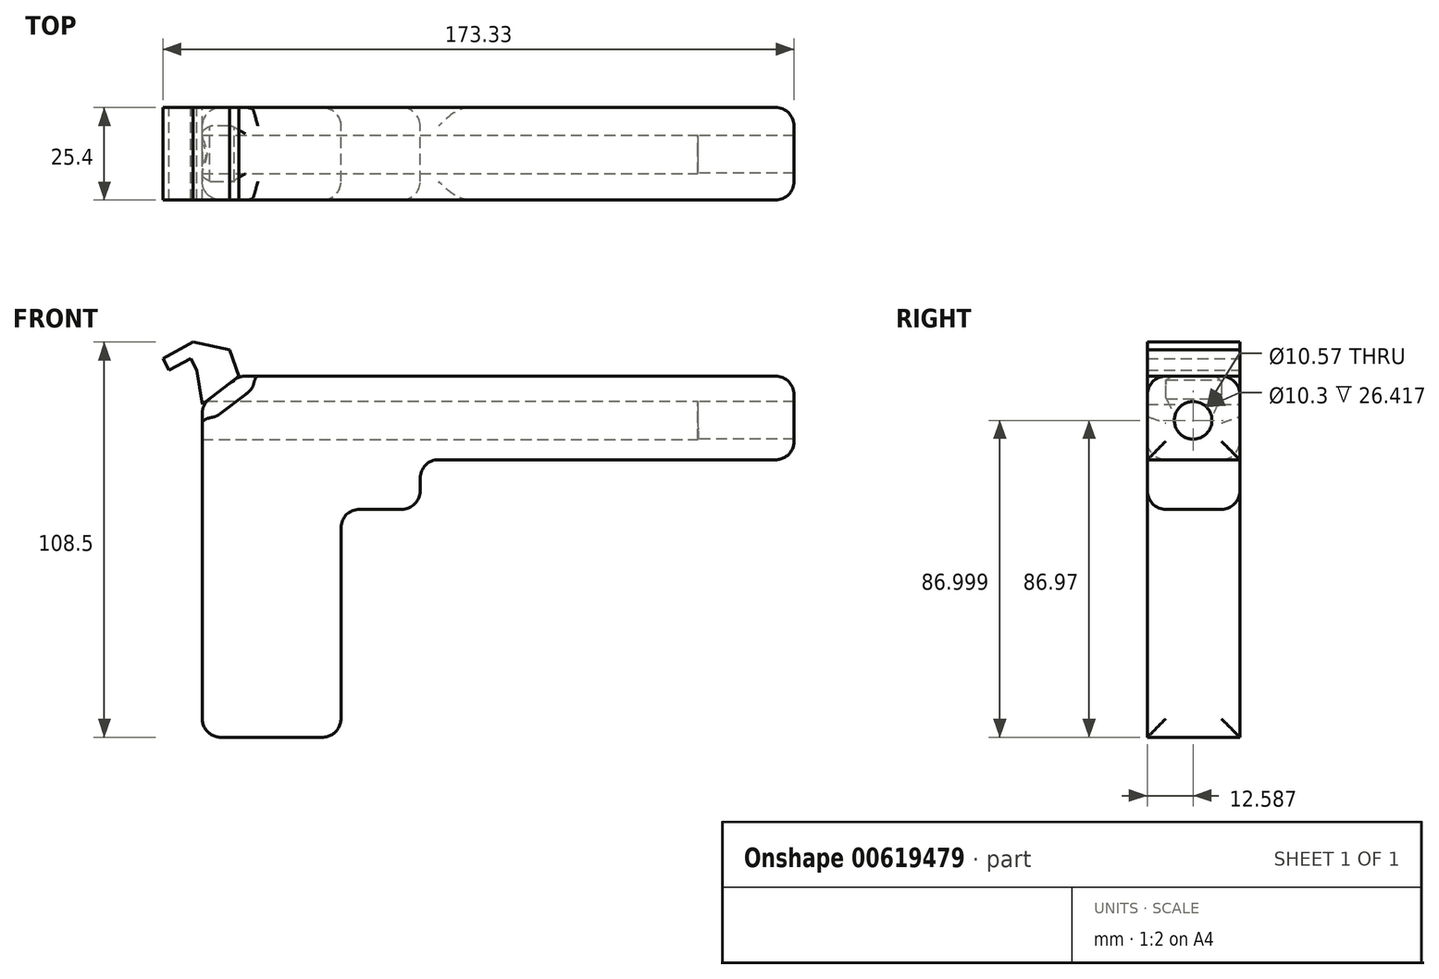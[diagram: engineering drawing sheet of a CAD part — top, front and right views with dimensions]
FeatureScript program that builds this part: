
annotation { "Feature Type Name" : "Feature", "Feature Type Description" : "" }
export const myFeature = defineFeature(function(context is Context, id is Id, definition is map)
    precondition{}
    {
        {
            var Q0;
            Q0=qCreatedBy(makeId("Front.planeOp"),FACE);
            var sketch = newSketch(context, id + "F0", { "sketchPlane" : qUnion([Q0])});
            skLineSegment(sketch, "E0", {"start": v(-59.82, 21.4) * mm, "end": v(-59.82, -54.8) * mm});
            skLineSegment(sketch, "E1", {"start": v(-21.72, -54.8) * mm, "end": v(-59.82, -54.8) * mm});
            skLineSegment(sketch, "E2", {"start": v(-59.82, 21.4) * mm, "end": v(-21.72, 21.4) * mm});
            skLineSegment(sketch, "E3", {"start": v(-59.82, 21.4) * mm, "end": v(-59.82, 36.64) * mm});
            skLineSegment(sketch, "E4", {"start": v(-59.82, 36.64) * mm, "end": v(-49.72, 44.33) * mm});
            skLineSegment(sketch, "E5", {"start": v(-49.72, 44.33) * mm, "end": v(102.68, 44.33) * mm});
            skLineSegment(sketch, "E6", {"start": v(102.68, 44.33) * mm, "end": v(102.68, 21.4) * mm});
            skLineSegment(sketch, "E7", {"start": v(102.68, 21.4) * mm, "end": v(77.28, 21.4) * mm});
            skLineSegment(sketch, "E8", {"start": v(-21.72, 21.4) * mm, "end": v(77.28, 21.4) * mm});
            skLineSegment(sketch, "E9", {"start": v(-19.87, 51.15) * mm, "end": v(-21.72, 51.15) * mm});
            skLineSegment(sketch, "E10", {"start": v(-20.2, 7.79) * mm, "end": v(0, 7.79) * mm});
            skLineSegment(sketch, "E11", {"start": v(0, 7.79) * mm, "end": v(0, 21.4) * mm});
            skLineSegment(sketch, "E12", {"start": v(-21.72, 21.4) * mm, "end": v(-17.5, 10.03) * mm});
            skLineSegment(sketch, "E13", {"start": v(-17.5, 10.03) * mm, "end": v(-14.94, 10.98) * mm});
            skLineSegment(sketch, "E14", {"start": v(-14.94, 10.98) * mm, "end": v(-11.42, 13.47) * mm});
            skLineSegment(sketch, "E15", {"start": v(-21.72, -54.8) * mm, "end": v(-21.72, 21.4) * mm});
            skLineSegment(sketch, "E16", {"start": v(-20.2, 7.79) * mm, "end": v(-21.72, 7.79) * mm});
            skLineSegment(sketch, "E17", {"start": v(-49.72, 44.33) * mm, "end": v(-52.32, 51.56) * mm});
            skLineSegment(sketch, "E18", {"start": v(-52.32, 51.56) * mm, "end": v(-62.32, 53.7) * mm});
            skLineSegment(sketch, "E19", {"start": v(-62.32, 53.7) * mm, "end": v(-70.65, 49.18) * mm});
            skLineSegment(sketch, "E20", {"start": v(-70.65, 49.18) * mm, "end": v(-68.9, 45.97) * mm});
            skLineSegment(sketch, "E21", {"start": v(-68.9, 45.97) * mm, "end": v(-63, 49.18) * mm});
            skLineSegment(sketch, "E22", {"start": v(-63, 49.18) * mm, "end": v(-61.27, 45.97) * mm});
            skLineSegment(sketch, "E23", {"start": v(-61.27, 45.97) * mm, "end": v(-59.82, 36.64) * mm});
            skSolve(sketch);
        }
        {
            var Q0;
            {var subQ0=sQuery(id+"F0.wireOp",EDGE,"E2");Q0=makeQuery(id+"F0.imprint","IMPRINT",FACE,{"disambiguationData":[TD([[makeQuery(id+"F0.imprint","IMPRINT",EDGE,{"derivedFrom":subQ0}),1.0]])]});}
            extrude(context, id + "F1", {"entities" : qUnion([Q0]), "depth" : 25.4 * mm, "offsetDistance" : 25.4 * mm});
        }
        {
            var Q0;
            Q0=makeQuery(id+"F0.imprint","IMPRINT",FACE,{"disambiguationData":[TD([[makeQuery(id+"F0.imprint","IMPRINT",EDGE,{"derivedFrom":sQuery(id+"F0.wireOp",EDGE,"E0")}),1.0]])]});
            extrude(context, id + "F2", {"entities" : qUnion([Q0]), "operationType" : NewBodyOperationType.ADD, "depth" : 25.4 * mm, "offsetDistance" : 25.4 * mm});
        }
        {
            var Q0;
            Q0=makeQuery(id+"F0.imprint","IMPRINT",FACE,{"disambiguationData":[TD([[makeQuery(id+"F0.imprint","IMPRINT",EDGE,{"derivedFrom":sQuery(id+"F0.wireOp",EDGE,"E10")}),1.0]])]});
            extrude(context, id + "F3", {"entities" : qUnion([Q0]), "operationType" : NewBodyOperationType.ADD, "depth" : 25.4 * mm, "offsetDistance" : 25.4 * mm});
        }
        {
            var Q0;
            Q0=makeQuery(id+"F1.opExtrude","CAP_EDGE",EDGE,{"disambiguationData":[OSD([sQuery(id+"F0.wireOp",EDGE,"E6")])],"isStart":true});
            var Q1;
            Q1=makeQuery(id+"F1.opExtrude","SWEPT_EDGE",EDGE,{"disambiguationData":[OSD([sQuery(id+"F0.wireOp",EDGE,"E5"),sQuery(id+"F0.wireOp",EDGE,"E6")])]});
            var Q2;
            Q2=makeQuery(id+"F1.opExtrude","CAP_EDGE",EDGE,{"disambiguationData":[OSD([sQuery(id+"F0.wireOp",EDGE,"E6")])],"isStart":false});
            var Q3;
            Q3=makeQuery(id+"F1.opExtrude","SWEPT_EDGE",EDGE,{"disambiguationData":[OSD([sQuery(id+"F0.wireOp",EDGE,"E6"),sQuery(id+"F0.wireOp",EDGE,"E7")])]});
            fillet(context, id + "F4", {"entities" : qUnion([Q0, Q1, Q2, Q3]), "radius" : 5.08 * mm, "tangentPropagation" : true, "allowEdgeOverflow" : false});
        }
        {
            var Q0;
            Q0=makeQuery(id+"F1.opExtrude","CAP_EDGE",EDGE,{"disambiguationData":[OSD([sQuery(id+"F0.wireOp",EDGE,"E4")])],"isStart":true});
            var Q1;
            Q1=makeQuery(id+"F1.opExtrude","CAP_EDGE",EDGE,{"disambiguationData":[OSD([sQuery(id+"F0.wireOp",EDGE,"E4")])],"isStart":false});
            chamfer(context, id + "F5", {"entities" : qUnion([Q0, Q1]), "width" : 5.08 * mm, "tangentPropagation" : true});
        }
        {
            var Q0;
            Q0=makeQuery(id+"F3.opExtrude","CAP_EDGE",EDGE,{"disambiguationData":[OSD([sQuery(id+"F0.wireOp",EDGE,"E11")])],"isStart":true});
            var Q1;
            Q1=makeQuery(id+"F3.opExtrude","CAP_EDGE",EDGE,{"disambiguationData":[OSD([sQuery(id+"F0.wireOp",EDGE,"E10"),sQuery(id+"F0.wireOp",EDGE,"E16")])],"isStart":true});
            var Q2;
            Q2=makeQuery(id+"F3.opExtrude","CAP_EDGE",EDGE,{"disambiguationData":[OSD([sQuery(id+"F0.wireOp",EDGE,"E11")])],"isStart":false});
            var Q3;
            Q3=makeQuery(id+"F3.opExtrude","CAP_EDGE",EDGE,{"disambiguationData":[OSD([sQuery(id+"F0.wireOp",EDGE,"E10"),sQuery(id+"F0.wireOp",EDGE,"E16")])],"isStart":false});
            var Q4;
            Q4=makeQuery(id+"F3.opExtrude","SWEPT_EDGE",EDGE,{"disambiguationData":[OSD([sQuery(id+"F0.wireOp",EDGE,"E10"),sQuery(id+"F0.wireOp",EDGE,"E11")])]});
            var Q5;
            Q5=makeQuery(id+"F3.opExtrude","SWEPT_FACE",FACE,{"disambiguationData":[OSD([sQuery(id+"F0.wireOp",EDGE,"E11")])]});
            var Q6;
            Q6=makeQuery(id+"F2.opExtrude","SWEPT_FACE",FACE,{"disambiguationData":[OSD([sQuery(id+"F0.wireOp",EDGE,"E15")])]});
            var Q7;
            Q7=makeQuery(id+"F2.boolean.opBoolean","MERGE",FACE,{"derivedFrom":[makeQuery(id+"F1.opExtrude","SWEPT_FACE",FACE,{"disambiguationData":[OSD([sQuery(id+"F0.wireOp",EDGE,"E3")])]}),makeQuery(id+"F2.opExtrude","SWEPT_FACE",FACE,{"disambiguationData":[OSD([sQuery(id+"F0.wireOp",EDGE,"E0")])]})]});
            var Q8;
            Q8=makeQuery(id+"F1.opExtrude","SWEPT_FACE",FACE,{"disambiguationData":[OSD([sQuery(id+"F0.wireOp",EDGE,"E5")])]});
            fillet(context, id + "F6", {"entities" : qUnion([Q0, Q1, Q2, Q3, Q4, Q5, Q6, Q7, Q8]), "radius" : 5.08 * mm, "tangentPropagation" : true, "allowEdgeOverflow" : false});
        }
        {
            var Q0;
            Q0=makeQuery(id+"F1.opExtrude","SWEPT_FACE",FACE,{"disambiguationData":[OSD([sQuery(id+"F0.wireOp",EDGE,"E4")])]});
            var sketch = newSketch(context, id + "F7", { "sketchPlane" : qUnion([Q0])});
            skLineSegment(sketch, "E24.bottom", {"start": v(-14.4, -5.45) * mm, "end": v(-21.74, -5.45) * mm});
            skLineSegment(sketch, "E24.top", {"start": v(-14.4, -20.32) * mm, "end": v(-21.74, -20.32) * mm});
            skLineSegment(sketch, "E24.left", {"start": v(-14.4, -5.45) * mm, "end": v(-14.4, -20.32) * mm});
            skLineSegment(sketch, "E24.right", {"start": v(-21.74, -5.45) * mm, "end": v(-21.74, -20.32) * mm});
            skLineSegment(sketch, "E25", {"start": v(-19, -13.14) * mm, "end": v(-18, -13.14) * mm});
            skPoint(sketch, "E25.endSnap0", {"position": v(-18, -9.1) * mm});
            skLineSegment(sketch, "E26", {"start": v(-18, -13.14) * mm, "end": v(-19, -13.14) * mm});
            skLineSegment(sketch, "E27", {"start": v(-18, -13.14) * mm, "end": v(-19, -12.26) * mm});
            skLineSegment(sketch, "E28", {"start": v(-18, -10.58) * mm, "end": v(-19, -12.26) * mm});
            skLineSegment(sketch, "E29", {"start": v(-18, -10.58) * mm, "end": v(-18, -13.14) * mm});
            skLineSegment(sketch, "E30", {"start": v(-19.53, -10.01) * mm, "end": v(-18, -10.58) * mm});
            skLineSegment(sketch, "E31", {"start": v(-19.72, -10.75) * mm, "end": v(-19, -12.26) * mm});
            skLineSegment(sketch, "E32", {"start": v(-19.33, -11.5) * mm, "end": v(-18, -10.58) * mm});
            skLineSegment(sketch, "E33", {"start": v(-19.33, -11.68) * mm, "end": v(-18, -13.14) * mm});
            skLineSegment(sketch, "E34", {"start": v(-19.91, -14.25) * mm, "end": v(-19.91, -15.54) * mm});
            skLineSegment(sketch, "E35", {"start": v(-19.91, -15.54) * mm, "end": v(-19.91, -14.25) * mm});
            skLineSegment(sketch, "E36", {"start": v(-19.14, -15.37) * mm, "end": v(-19.91, -14.25) * mm});
            skLineSegment(sketch, "E37", {"start": v(-19.14, -15.37) * mm, "end": v(-18, -13.14) * mm});
            skLineSegment(sketch, "E38", {"start": v(-17.78, -14.08) * mm, "end": v(-19.14, -15.37) * mm});
            skLineSegment(sketch, "E39", {"start": v(-17.58, -12.24) * mm, "end": v(-18, -10.58) * mm});
            skLineSegment(sketch, "E40", {"start": v(-19.91, -13.15) * mm, "end": v(-19, -12.26) * mm});
            skLineSegment(sketch, "E41", {"start": v(-20.3, -11.85) * mm, "end": v(-18, -13.14) * mm});
            skSolve(sketch);
        }
        {
            var Q0;
            Q0 = qSketchRegion(id + "F7", true);
            extrude(context, id + "F8", {"entities" : qUnion([Q0]), "operationType" : NewBodyOperationType.ADD, "oppositeDirection" : true, "depth" : 29.72 * mm, "offsetDistance" : 25.4 * mm});
        }
        {
            var Q0;
            Q0=makeQuery(id+"F0.imprint","IMPRINT",FACE,{"disambiguationData":[TD([[makeQuery(id+"F0.imprint","IMPRINT",EDGE,{"derivedFrom":sQuery(id+"F0.wireOp",EDGE,"E4")}),1.0]])]});
            extrude(context, id + "F9", {"entities" : qUnion([Q0]), "operationType" : NewBodyOperationType.ADD, "depth" : 25.4 * mm, "offsetDistance" : 25.4 * mm});
        }
        {
            var Q0;
            Q0=qCreatedBy(makeId("Right.planeOp"),FACE);
            var sketch = newSketch(context, id + "F10", { "sketchPlane" : qUnion([Q0])});
            skCircle(sketch, "E42", {"center": v(-12.81, 32.17) * mm, "radius": 5.28 * mm});
            skSolve(sketch);
        }
        {
            var Q0;
            Q0=sQuery(id+"F10.wireOp",VERTEX,"E42.center");
            var Q1;
            Q1=makeQuery(id+"F1.opExtrude","SWEPT_BODY",BODY,{"disambiguationData":[OSD([sQuery(id+"F0.wireOp",EDGE,"E2"),sQuery(id+"F0.wireOp",EDGE,"E3"),sQuery(id+"F0.wireOp",EDGE,"E4"),sQuery(id+"F0.wireOp",EDGE,"E5"),sQuery(id+"F0.wireOp",EDGE,"E6"),sQuery(id+"F0.wireOp",EDGE,"E7"),sQuery(id+"F0.wireOp",EDGE,"E8")])]});
            hole(context, id + "F11", {"style" : HoleStyle.SIMPLE, "endStyle" : HoleEndStyle.BLIND, "holeDiameter" : 10.57 * mm, "majorDiameter" : 6.35 * mm, "holeDepth" : 76.2 * mm, "isTappedThrough" : true, "tappedDepth" : 12.7 * mm, "tapClearance" : 3, "locations" : qUnion([Q0]), "scope" : qUnion([Q1])});
        }
        {
            var Q0;
            Q0=sQuery(id+"F10.wireOp",VERTEX,"E42.center");
            var Q1;
            Q1=makeQuery(id+"F1.opExtrude","SWEPT_BODY",BODY,{"disambiguationData":[OSD([sQuery(id+"F0.wireOp",EDGE,"E2"),sQuery(id+"F0.wireOp",EDGE,"E3"),sQuery(id+"F0.wireOp",EDGE,"E4"),sQuery(id+"F0.wireOp",EDGE,"E5"),sQuery(id+"F0.wireOp",EDGE,"E6"),sQuery(id+"F0.wireOp",EDGE,"E7"),sQuery(id+"F0.wireOp",EDGE,"E8")])]});
            hole(context, id + "F12", {"style" : HoleStyle.SIMPLE, "endStyle" : HoleEndStyle.BLIND, "oppositeDirection" : true, "holeDiameter" : 10.57 * mm, "majorDiameter" : 6.35 * mm, "holeDepth" : 76.2 * mm, "isTappedThrough" : true, "tappedDepth" : 12.7 * mm, "tapClearance" : 3, "locations" : qUnion([Q0]), "scope" : qUnion([Q1])});
        }
        {
            var Q0;
            Q0=qCreatedBy(makeId("Right.planeOp"),FACE);
            var sketch = newSketch(context, id + "F13", { "sketchPlane" : qUnion([Q0])});
            skCircle(sketch, "E43", {"center": v(-12.81, 32.2) * mm, "radius": 5.27 * mm});
            skSolve(sketch);
        }
        {
            var Q0;
            Q0=sQuery(id+"F13.wireOp",VERTEX,"E43.center");
            var Q1;
            Q1=makeQuery(id+"F1.opExtrude","SWEPT_BODY",BODY,{"disambiguationData":[OSD([sQuery(id+"F0.wireOp",EDGE,"E2"),sQuery(id+"F0.wireOp",EDGE,"E3"),sQuery(id+"F0.wireOp",EDGE,"E4"),sQuery(id+"F0.wireOp",EDGE,"E5"),sQuery(id+"F0.wireOp",EDGE,"E6"),sQuery(id+"F0.wireOp",EDGE,"E7"),sQuery(id+"F0.wireOp",EDGE,"E8")])]});
            hole(context, id + "F14", {"style" : HoleStyle.SIMPLE, "endStyle" : HoleEndStyle.BLIND, "oppositeDirection" : true, "holeDiameter" : 10.3 * mm, "majorDiameter" : 5 * mm, "holeDepth" : 9000 * mm, "isTappedThrough" : true, "tappedDepth" : 12.7 * mm, "tapClearance" : 3, "locations" : qUnion([Q0]), "scope" : qUnion([Q1])});
        }
    });
